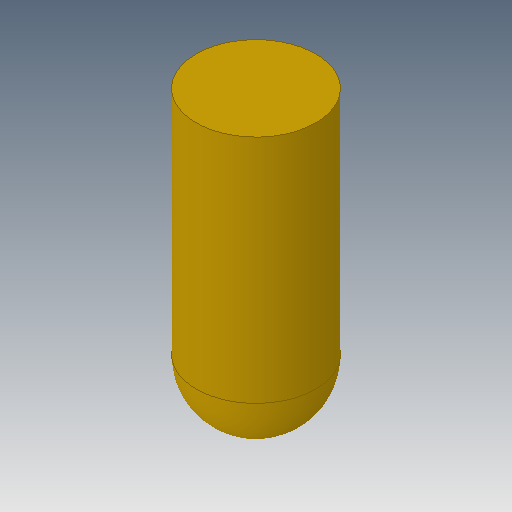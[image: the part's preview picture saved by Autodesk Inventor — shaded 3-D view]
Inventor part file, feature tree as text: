
AUTODESK INVENTOR PART (.ipt)
format: ipt  version: 2018 (Build 220112000, 112)  size: 114,176 bytes
history: native  units: mm
features: extrude x1, fillet x1, sketch x1
ambient origin geometry x8: Origin, YZ Plane, XZ Plane, XY Plane, X Axis, Y Axis, Z Axis, Center Point
bodies: Solid1 (feature_tree)
feature tree (3):
  extrude  "Extrusion1"  Depth=2.6mm TaperAngle=0.0deg
  fillet  "Fillet1"  Radius=0.535mm
  sketch  "Sketch1"  dims[d0=1.07mm d1=2.6mm d2=0.0mm d3=0.535mm]
